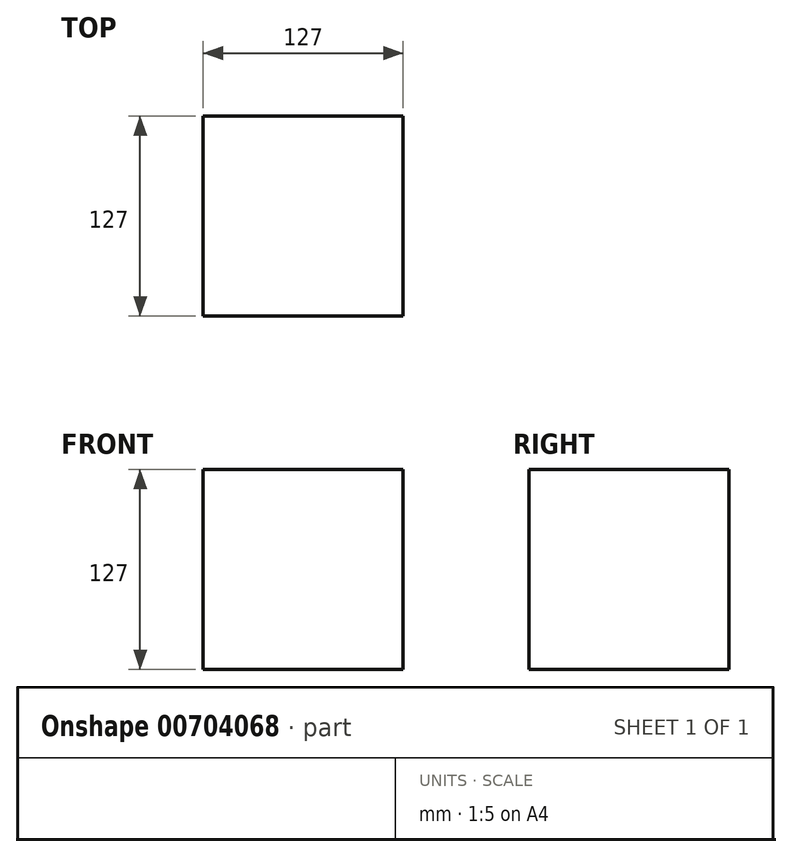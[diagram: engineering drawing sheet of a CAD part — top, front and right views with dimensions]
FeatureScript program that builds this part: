
annotation { "Feature Type Name" : "Feature", "Feature Type Description" : "" }
export const myFeature = defineFeature(function(context is Context, id is Id, definition is map)
    precondition{}
    {
        {
            var Q0;
            Q0=qCreatedBy(makeId("Front.planeOp"),FACE);
            var sketch = newSketch(context, id + "F0", { "sketchPlane" : qUnion([Q0])});
            skLineSegment(sketch, "E0.bottom", {"start": v(-107.64, 121.75) * mm, "end": v(19.36, 121.75) * mm});
            skLineSegment(sketch, "E0.top", {"start": v(-107.64, -5.25) * mm, "end": v(19.36, -5.25) * mm});
            skLineSegment(sketch, "E0.left", {"start": v(-107.64, 121.75) * mm, "end": v(-107.64, -5.25) * mm});
            skLineSegment(sketch, "E0.right", {"start": v(19.36, 121.75) * mm, "end": v(19.36, -5.25) * mm});
            skSolve(sketch);
        }
        {
            var Q0;
            Q0 = qSketchRegion(id + "F0", true);
            extrude(context, id + "F1", {"entities" : qUnion([Q0]), "depth" : 127 * mm, "offsetDistance" : 25.4 * mm});
        }
    });
